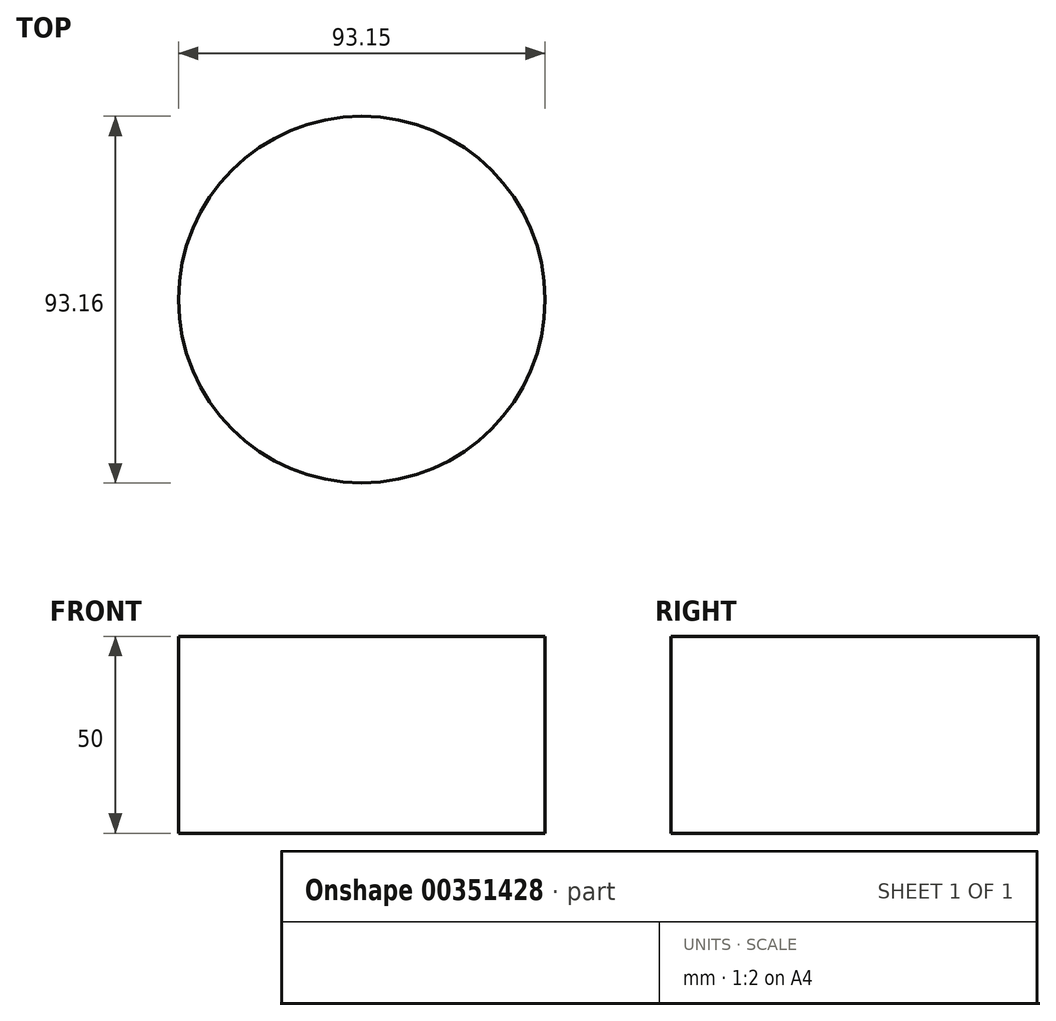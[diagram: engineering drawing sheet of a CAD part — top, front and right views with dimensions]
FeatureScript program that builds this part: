
annotation { "Feature Type Name" : "Feature", "Feature Type Description" : "" }
export const myFeature = defineFeature(function(context is Context, id is Id, definition is map)
    precondition{}
    {
        {
            var Q0;
            Q0=qCreatedBy(makeId("Top.planeOp"),FACE);
            var sketch = newSketch(context, id + "F0", { "sketchPlane" : qUnion([Q0])});
            skCircle(sketch, "E0", {"center": v(-53.9, 0) * mm, "radius": 46.58 * mm});
            skSolve(sketch);
        }
        {
            var Q0;
            Q0 = qSketchRegion(id + "F0", true);
            extrude(context, id + "F1", {"entities" : qUnion([Q0]), "depth" : 50 * mm});
        }
    });
